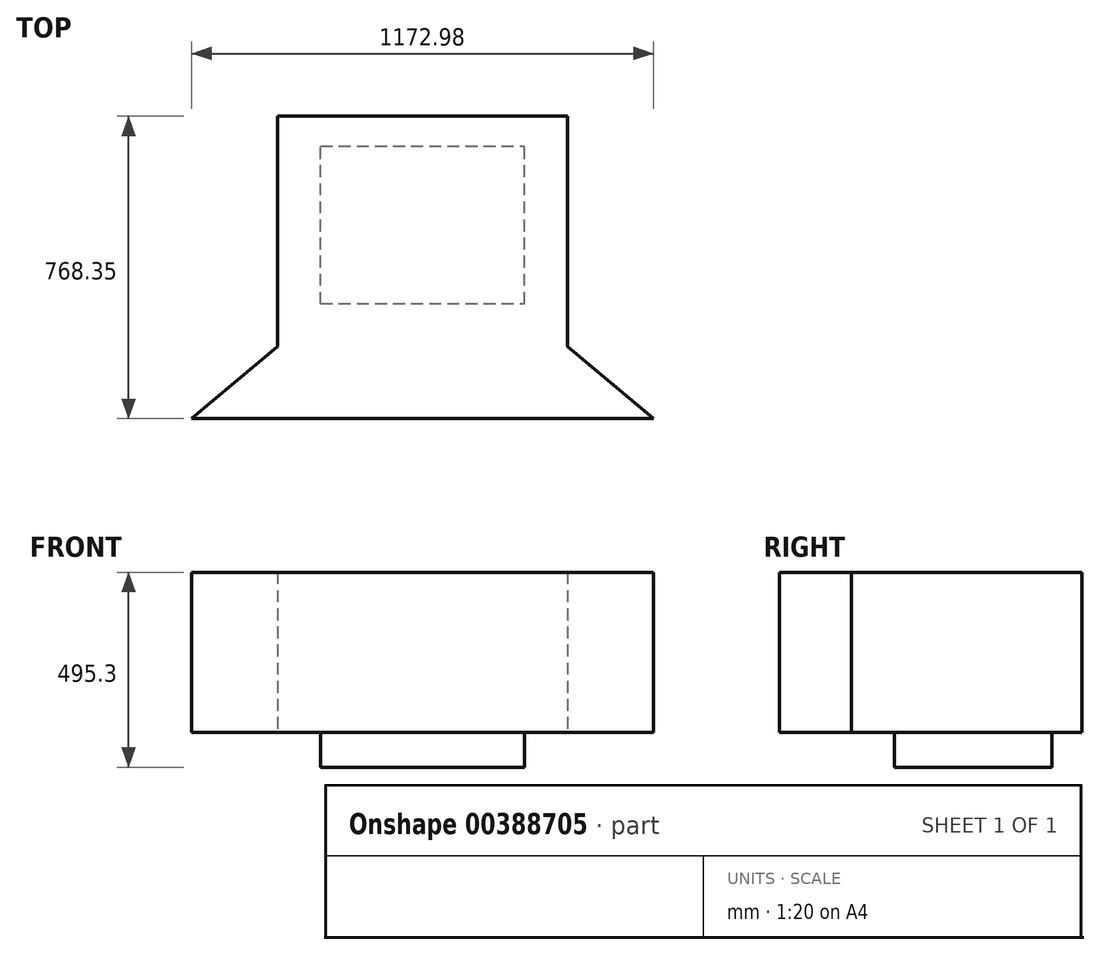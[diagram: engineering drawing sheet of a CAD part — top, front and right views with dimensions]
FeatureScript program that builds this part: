
annotation { "Feature Type Name" : "Feature", "Feature Type Description" : "" }
export const myFeature = defineFeature(function(context is Context, id is Id, definition is map)
    precondition{}
    {
        {
            var Q0;
            Q0=qCreatedBy(makeId("Top.planeOp"),FACE);
            var sketch = newSketch(context, id + "F0", { "sketchPlane" : qUnion([Q0])});
            skLineSegment(sketch, "E0.bottom", {"start": v(0, -23.53) * mm, "end": v(517.52, -23.53) * mm});
            skLineSegment(sketch, "E0.top", {"start": v(0, 376.52) * mm, "end": v(517.52, 376.52) * mm});
            skLineSegment(sketch, "E0.left", {"start": v(0, -23.53) * mm, "end": v(0, 376.52) * mm});
            skLineSegment(sketch, "E0.right", {"start": v(517.52, -23.53) * mm, "end": v(517.52, 376.52) * mm});
            skSolve(sketch);
        }
        {
            var Q0;
            Q0 = qSketchRegion(id + "F0", true);
            extrude(context, id + "F1", {"entities" : qUnion([Q0]), "depth" : 88.9 * mm});
        }
        {
            var Q0;
            Q0=makeQuery(id+"F1.opExtrude","CAP_FACE",FACE,{"disambiguationData":[OSD([sQuery(id+"F0.wireOp",EDGE,"E0.bottom"),sQuery(id+"F0.wireOp",EDGE,"E0.top"),sQuery(id+"F0.wireOp",EDGE,"E0.left"),sQuery(id+"F0.wireOp",EDGE,"E0.right")])],"isStart":false});
            var sketch = newSketch(context, id + "F2", { "sketchPlane" : qUnion([Q0])});
            skLineSegment(sketch, "E1.bottom", {"start": v(627.06, -315.63) * mm, "end": v(-109.54, -315.63) * mm});
            skLineSegment(sketch, "E1.left", {"start": v(627.06, -315.63) * mm, "end": v(627.06, 452.72) * mm});
            skLineSegment(sketch, "E1.right", {"start": v(-109.54, -315.63) * mm, "end": v(-109.54, 452.72) * mm});
            skPoint(sketch, "E1.middle", {"position": v(258.76, 176.5) * mm});
            skPoint(sketch, "E1.middle.positionSnap0", {"position": v(258.76, 376.52) * mm});
            skPoint(sketch, "E1.middle.positionSnap1", {"position": v(0, 176.5) * mm});
            skPoint(sketch, "E1.centerSnap0", {"position": v(258.76, 376.52) * mm});
            skPoint(sketch, "E1.centerSnap1", {"position": v(0, 176.5) * mm});
            skLineSegment(sketch, "E2", {"start": v(-109.54, 452.72) * mm, "end": v(627.06, 452.72) * mm});
            skLineSegment(sketch, "E3", {"start": v(258.76, 452.72) * mm, "end": v(258.76, -315.63) * mm, "construction": true});
            skLineSegment(sketch, "E4", {"start": v(258.76, 176.5) * mm, "end": v(-327.73, -315.63) * mm});
            skLineSegment(sketch, "E5", {"start": v(258.76, 176.5) * mm, "end": v(845.25, -315.63) * mm});
            skLineSegment(sketch, "E6", {"start": v(-327.73, -315.63) * mm, "end": v(845.25, -315.63) * mm});
            skSolve(sketch);
        }
        {
            var Q0;
            Q0 = qSketchRegion(id + "F2", true);
            extrude(context, id + "F3", {"entities" : qUnion([Q0]), "operationType" : NewBodyOperationType.ADD, "depth" : 406.4 * mm});
        }
    });
